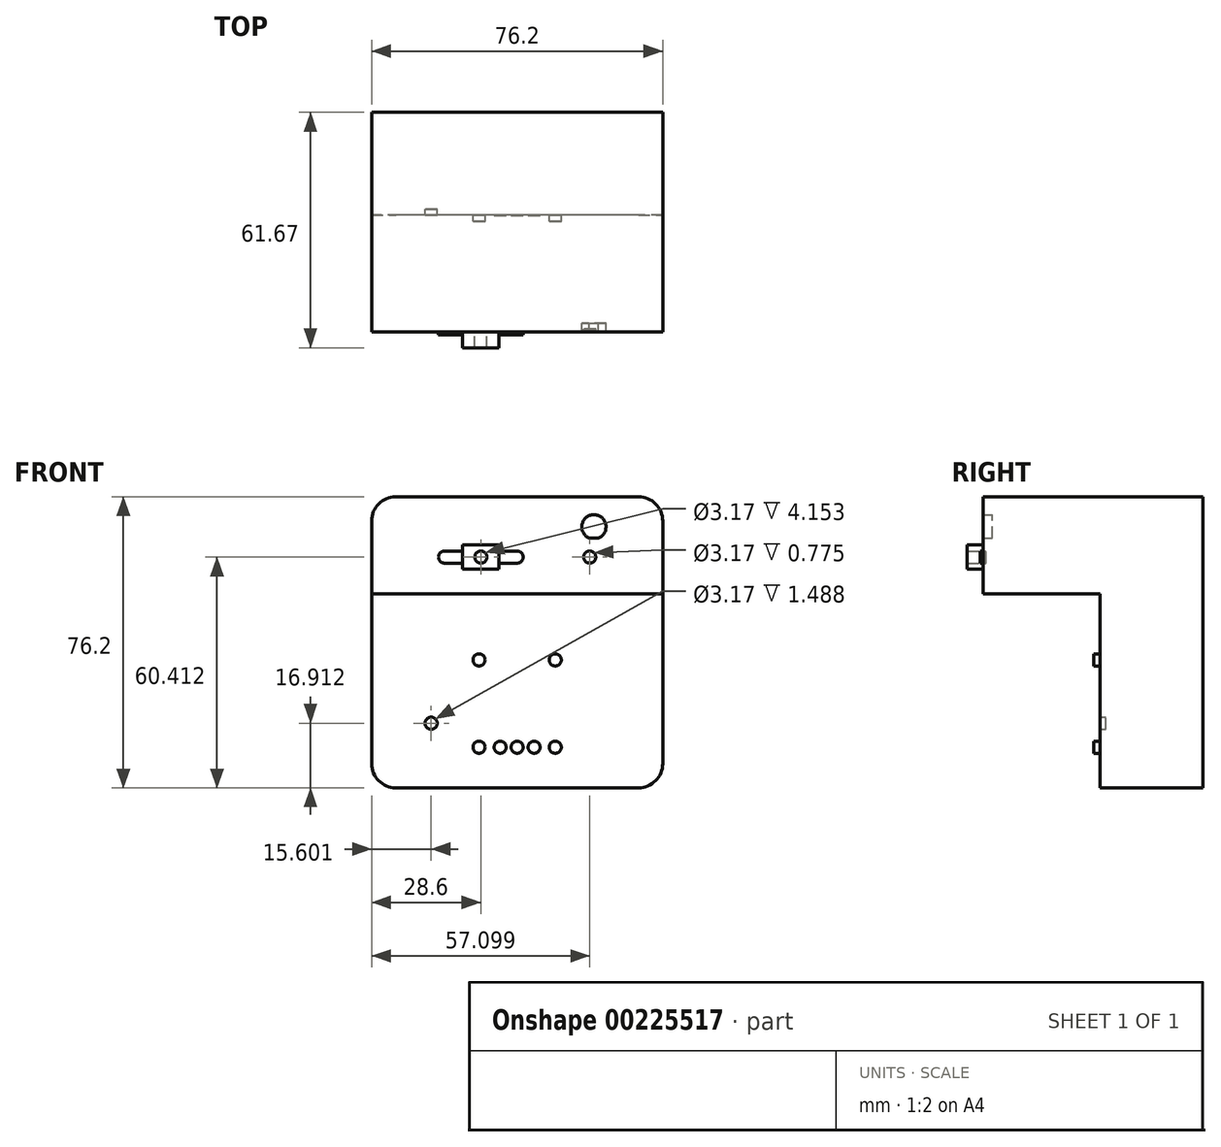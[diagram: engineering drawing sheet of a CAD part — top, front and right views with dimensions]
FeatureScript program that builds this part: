
annotation { "Feature Type Name" : "Feature", "Feature Type Description" : "" }
export const myFeature = defineFeature(function(context is Context, id is Id, definition is map)
    precondition{}
    {
        {
            var Q0;
            Q0=qCreatedBy(makeId("Front.planeOp"),FACE);
            var sketch = newSketch(context, id + "F0", { "sketchPlane" : qUnion([Q0])});
            skLineSegment(sketch, "E0.bottom", {"start": v(38.1, -38.1) * mm, "end": v(-38.1, -38.1) * mm});
            skLineSegment(sketch, "E0.top", {"start": v(38.1, 38.1) * mm, "end": v(-38.1, 38.1) * mm});
            skLineSegment(sketch, "E0.left", {"start": v(38.1, -38.1) * mm, "end": v(38.1, 38.1) * mm});
            skLineSegment(sketch, "E0.right", {"start": v(-38.1, -38.1) * mm, "end": v(-38.1, 38.1) * mm});
            skPoint(sketch, "E0.middle", {"position": v(0, 0) * mm});
            skCircle(sketch, "E1", {"center": v(0, 22.31) * mm, "radius": 1.59 * mm});
            skCircle(sketch, "E2", {"center": v(-19, 22.31) * mm, "radius": 1.59 * mm});
            skCircle(sketch, "E3.MirrorC", {"center": v(19, 22.31) * mm, "radius": 1.59 * mm});
            skLineSegment(sketch, "E4", {"start": v(0, 38.1) * mm, "end": v(0, -38.1) * mm, "construction": true});
            skLineSegment(sketch, "E5", {"start": v(-19, 22.31) * mm, "end": v(19, 22.31) * mm, "construction": true});
            skCircle(sketch, "E6", {"center": v(-4.45, -27.48) * mm, "radius": 1.59 * mm});
            skLineSegment(sketch, "E7.0", {"start": v(-9.5, 38.1) * mm, "end": v(-9.5, -38.1) * mm, "construction": true});
            skCircle(sketch, "E8", {"center": v(-9.98, -27.48) * mm, "radius": 1.59 * mm});
            skCircle(sketch, "E9", {"center": v(-9.98, -4.62) * mm, "radius": 1.59 * mm});
            skLineSegment(sketch, "E10.MirrorCS", {"start": v(9.5, 38.1) * mm, "end": v(9.5, -38.1) * mm, "construction": true});
            skCircle(sketch, "E11.MirrorC", {"center": v(9.98, -4.62) * mm, "radius": 1.59 * mm});
            skCircle(sketch, "E12.MirrorC", {"center": v(9.98, -27.48) * mm, "radius": 1.59 * mm});
            skCircle(sketch, "E13.MirrorC", {"center": v(4.45, -27.48) * mm, "radius": 1.59 * mm});
            skLineSegment(sketch, "E14", {"start": v(-8.39, -27.48) * mm, "end": v(-8.39, -4.62) * mm, "construction": true});
            skLineSegment(sketch, "E15", {"start": v(-38.1, 0) * mm, "end": v(38.1, 0) * mm});
            skSolve(sketch);
        }
        {
            var Q0;
            {var subQ1=sQuery(id+"F0.wireOp",EDGE,"E0.bottom");Q0=makeQuery(id+"F0.imprint","IMPRINT",FACE,{"disambiguationData":[TD([[makeQuery(id+"F0.imprint","IMPRINT",EDGE,{"derivedFrom":subQ1}),-1.0]])]});}
            var Q1;
            {var subQ1=sQuery(id+"F0.wireOp",EDGE,"E0.top");Q1=makeQuery(id+"F0.imprint","IMPRINT",FACE,{"disambiguationData":[TD([[makeQuery(id+"F0.imprint","IMPRINT",EDGE,{"derivedFrom":subQ1}),1.0]])]});}
            extrude(context, id + "F1", {"entities" : qUnion([Q0, Q1]), "oppositeDirection" : true, "depth" : 25.4 * mm});
        }
        {
            var Q0;
            Q0=qCreatedBy(makeId("Front.planeOp"),FACE);
            var sketch = newSketch(context, id + "F2", { "sketchPlane" : qUnion([Q0])});
            skCircle(sketch, "E16.0", {"center": v(-9.98, -4.62) * mm, "radius": 1.59 * mm});
            skCircle(sketch, "E17.0", {"center": v(9.98, -4.62) * mm, "radius": 1.59 * mm});
            skCircle(sketch, "E18.0", {"center": v(9.98, -27.48) * mm, "radius": 1.59 * mm});
            skCircle(sketch, "E19.0", {"center": v(4.45, -27.48) * mm, "radius": 1.59 * mm});
            skCircle(sketch, "E20.0", {"center": v(-4.45, -27.48) * mm, "radius": 1.59 * mm});
            skCircle(sketch, "E21.0", {"center": v(-9.98, -27.48) * mm, "radius": 1.59 * mm});
            skSolve(sketch);
        }
        {
            var Q0;
            Q0=makeQuery(id+"F2.imprint","IMPRINT",FACE,{"disambiguationData":[TD([[makeQuery(id+"F2.imprint","IMPRINT",EDGE,{"derivedFrom":sQuery(id+"F2.wireOp",EDGE,"E17.0")}),1.0]])]});
            var Q1;
            Q1=makeQuery(id+"F2.imprint","IMPRINT",FACE,{"disambiguationData":[TD([[makeQuery(id+"F2.imprint","IMPRINT",EDGE,{"derivedFrom":sQuery(id+"F2.wireOp",EDGE,"E16.0")}),1.0]])]});
            var Q2;
            Q2=makeQuery(id+"F2.imprint","IMPRINT",FACE,{"disambiguationData":[TD([[makeQuery(id+"F2.imprint","IMPRINT",EDGE,{"derivedFrom":sQuery(id+"F2.wireOp",EDGE,"E21.0")}),1.0]])]});
            var Q3;
            Q3=makeQuery(id+"F2.imprint","IMPRINT",FACE,{"disambiguationData":[TD([[makeQuery(id+"F2.imprint","IMPRINT",EDGE,{"derivedFrom":sQuery(id+"F2.wireOp",EDGE,"E20.0")}),1.0]])]});
            var Q4;
            Q4=makeQuery(id+"F2.imprint","IMPRINT",FACE,{"disambiguationData":[TD([[makeQuery(id+"F2.imprint","IMPRINT",EDGE,{"derivedFrom":sQuery(id+"F2.wireOp",EDGE,"E19.0")}),1.0]])]});
            var Q5;
            Q5=makeQuery(id+"F2.imprint","IMPRINT",FACE,{"disambiguationData":[TD([[makeQuery(id+"F2.imprint","IMPRINT",EDGE,{"derivedFrom":sQuery(id+"F2.wireOp",EDGE,"E18.0")}),1.0]])]});
            extrude(context, id + "F3", {"entities" : qUnion([Q0, Q1, Q2, Q3, Q4, Q5]), "operationType" : NewBodyOperationType.ADD, "depth" : 1.59 * mm});
        }
        {
            var Q0;
            Q0=qCreatedBy(makeId("Front.planeOp"),FACE);
            var sketch = newSketch(context, id + "F4", { "sketchPlane" : qUnion([Q0])});
            skCircle(sketch, "E22.0", {"center": v(-19, 22.31) * mm, "radius": 1.59 * mm});
            skCircle(sketch, "E23.0", {"center": v(0, 22.31) * mm, "radius": 1.59 * mm});
            skCircle(sketch, "E24.0", {"center": v(19, 22.31) * mm, "radius": 1.59 * mm});
            skSolve(sketch);
        }
        {
            var Q0;
            Q0 = qSketchRegion(id + "F4", true);
            extrude(context, id + "F5", {"entities" : qUnion([Q0]), "operationType" : NewBodyOperationType.ADD, "depth" : 31.35 * mm});
        }
        {
            var Q0;
            Q0=qCreatedBy(makeId("Front.planeOp"),FACE);
            var sketch = newSketch(context, id + "F6", { "sketchPlane" : qUnion([Q0])});
            skLineSegment(sketch, "E25.0", {"start": v(38.1, 38.1) * mm, "end": v(-38.1, 38.1) * mm});
            skLineSegment(sketch, "E26.0", {"start": v(-38.1, -38.1) * mm, "end": v(-38.1, 38.1) * mm});
            skLineSegment(sketch, "E27.0", {"start": v(38.1, -38.1) * mm, "end": v(38.1, 38.1) * mm});
            skLineSegment(sketch, "E28", {"start": v(-38.1, 0) * mm, "end": v(38.1, 0) * mm});
            skSolve(sketch);
        }
        {
            var Q0;
            {var subQ0=sQuery(id+"F6.wireOp",EDGE,"E25.0");Q0=makeQuery(id+"F6.imprint","IMPRINT",FACE,{"disambiguationData":[TD([[makeQuery(id+"F6.imprint","IMPRINT",EDGE,{"derivedFrom":subQ0}),1.0]])]});}
            extrude(context, id + "F7", {"entities" : qUnion([Q0]), "operationType" : NewBodyOperationType.ADD, "depth" : 29.76 * mm});
        }
        {
            var Q0;
            Q0=makeQuery(id+"F3.opExtrude","CAP_FACE",FACE,{"disambiguationData":[OSD([sQuery(id+"F2.wireOp",EDGE,"E21.0")])],"isStart":false});
            var sketch = newSketch(context, id + "F8", { "sketchPlane" : qUnion([Q0])});
            skCircle(sketch, "E29.0", {"center": v(-9.98, -27.48) * mm, "radius": 1.59 * mm});
            skCircle(sketch, "E30.0.0", {"center": v(-9.98, -4.62) * mm, "radius": 1.59 * mm});
            skCircle(sketch, "E31.0.0", {"center": v(9.98, -4.62) * mm, "radius": 1.59 * mm});
            skCircle(sketch, "E32.0.0", {"center": v(9.98, -27.48) * mm, "radius": 1.59 * mm});
            skSolve(sketch);
        }
        {
            var Q0;
            Q0=makeQuery(id+"F8.imprint","IMPRINT",FACE,{"disambiguationData":[TD([[makeQuery(id+"F8.imprint","IMPRINT",EDGE,{"derivedFrom":sQuery(id+"F8.wireOp",EDGE,"E30.0.0")}),1.0]])]});
            var Q1;
            Q1=makeQuery(id+"F8.imprint","IMPRINT",FACE,{"disambiguationData":[TD([[makeQuery(id+"F8.imprint","IMPRINT",EDGE,{"derivedFrom":sQuery(id+"F8.wireOp",EDGE,"E29.0")}),1.0]])]});
            var Q2;
            Q2=makeQuery(id+"F8.imprint","IMPRINT",FACE,{"disambiguationData":[TD([[makeQuery(id+"F8.imprint","IMPRINT",EDGE,{"derivedFrom":sQuery(id+"F8.wireOp",EDGE,"E32.0.0")}),1.0]])]});
            var Q3;
            Q3=makeQuery(id+"F8.imprint","IMPRINT",FACE,{"disambiguationData":[TD([[makeQuery(id+"F8.imprint","IMPRINT",EDGE,{"derivedFrom":sQuery(id+"F8.wireOp",EDGE,"E31.0.0")}),1.0]])]});
            extrude(context, id + "F9", {"entities" : qUnion([Q0, Q1, Q2, Q3]), "operationType" : NewBodyOperationType.ADD, "depth" : 1.59 * mm});
        }
        {
            var Q0;
            Q0=makeQuery(id+"F1.opExtrude","CAP_FACE",FACE,{"disambiguationData":[OSD([sQuery(id+"F0.wireOp",EDGE,"E0.bottom"),sQuery(id+"F0.wireOp",EDGE,"E0.top"),sQuery(id+"F0.wireOp",EDGE,"E0.left"),sQuery(id+"F0.wireOp",EDGE,"E0.right"),sQuery(id+"F0.wireOp",EDGE,"E1"),sQuery(id+"F0.wireOp",EDGE,"E2"),sQuery(id+"F0.wireOp",EDGE,"E3.MirrorC"),sQuery(id+"F0.wireOp",EDGE,"E6"),sQuery(id+"F0.wireOp",EDGE,"E8"),sQuery(id+"F0.wireOp",EDGE,"E9"),sQuery(id+"F0.wireOp",EDGE,"E11.MirrorC"),sQuery(id+"F0.wireOp",EDGE,"E12.MirrorC"),sQuery(id+"F0.wireOp",EDGE,"E13.MirrorC")])],"isStart":false});
            var sketch = newSketch(context, id + "F10", { "sketchPlane" : qUnion([Q0])});
            skCircle(sketch, "E33.0", {"center": v(9.98, -27.48) * mm, "radius": 1.59 * mm});
            skCircle(sketch, "E34.0", {"center": v(4.45, -27.48) * mm, "radius": 1.59 * mm});
            skCircle(sketch, "E35.0", {"center": v(-4.45, -27.48) * mm, "radius": 1.59 * mm});
            skCircle(sketch, "E36.0", {"center": v(-9.98, -27.48) * mm, "radius": 1.59 * mm});
            skCircle(sketch, "E37.0", {"center": v(9.98, -4.62) * mm, "radius": 1.59 * mm});
            skCircle(sketch, "E38.0", {"center": v(-9.98, -4.62) * mm, "radius": 1.59 * mm});
            skCircle(sketch, "E39.0", {"center": v(19, 22.31) * mm, "radius": 1.59 * mm});
            skCircle(sketch, "E40.0", {"center": v(0, 22.31) * mm, "radius": 1.59 * mm});
            skCircle(sketch, "E41.0", {"center": v(-19, 22.31) * mm, "radius": 1.59 * mm});
            skSolve(sketch);
        }
        {
            var Q0;
            Q0 = qSketchRegion(id + "F10", true);
            extrude(context, id + "F11", {"entities" : qUnion([Q0]), "operationType" : NewBodyOperationType.ADD, "endBound" : BoundingType.UP_TO_NEXT, "oppositeDirection" : true, "depth" : 25.4 * mm});
        }
        {
            var Q0;
            Q0=makeQuery(id+"F7.opExtrude","CAP_FACE",FACE,{"disambiguationData":[OSD([sQuery(id+"F6.wireOp",EDGE,"E25.0"),sQuery(id+"F6.wireOp",EDGE,"E26.0"),sQuery(id+"F6.wireOp",EDGE,"E27.0"),sQuery(id+"F6.wireOp",EDGE,"E28")])],"isStart":false});
            var sketch = newSketch(context, id + "F12", { "sketchPlane" : qUnion([Q0])});
            skLineSegment(sketch, "E42.0", {"start": v(-38.1, 0) * mm, "end": v(38.1, 0) * mm});
            skLineSegment(sketch, "E43.0", {"start": v(-38.1, 0) * mm, "end": v(-38.1, 12.7) * mm});
            skLineSegment(sketch, "E44.0", {"start": v(38.1, 0) * mm, "end": v(38.1, 12.7) * mm});
            skLineSegment(sketch, "E45", {"start": v(-38.1, 12.7) * mm, "end": v(38.1, 12.7) * mm});
            skPoint(sketch, "E46.orphan", {"position": v(-38.1, 38.1) * mm});
            skPoint(sketch, "E47.orphan", {"position": v(38.1, 38.1) * mm});
            skSolve(sketch);
        }
        {
            var Q0;
            Q0=makeQuery(id+"F12.imprint","IMPRINT",FACE,{"disambiguationData":[TD([[makeQuery(id+"F12.imprint","IMPRINT",EDGE,{"derivedFrom":sQuery(id+"F12.wireOp",EDGE,"E42.0")}),1.0]])]});
            var Q1;
            Q1=makeQuery(id+"F1.opExtrude","CAP_FACE",FACE,{"disambiguationData":[OSD([sQuery(id+"F0.wireOp",EDGE,"E0.bottom"),sQuery(id+"F0.wireOp",EDGE,"E0.top"),sQuery(id+"F0.wireOp",EDGE,"E0.left"),sQuery(id+"F0.wireOp",EDGE,"E0.right"),sQuery(id+"F0.wireOp",EDGE,"E1"),sQuery(id+"F0.wireOp",EDGE,"E2"),sQuery(id+"F0.wireOp",EDGE,"E3.MirrorC"),sQuery(id+"F0.wireOp",EDGE,"E6"),sQuery(id+"F0.wireOp",EDGE,"E8"),sQuery(id+"F0.wireOp",EDGE,"E9"),sQuery(id+"F0.wireOp",EDGE,"E11.MirrorC"),sQuery(id+"F0.wireOp",EDGE,"E12.MirrorC"),sQuery(id+"F0.wireOp",EDGE,"E13.MirrorC")])],"isStart":true});
            extrude(context, id + "F13", {"entities" : qUnion([Q0]), "operationType" : NewBodyOperationType.REMOVE, "endBound" : BoundingType.UP_TO_SURFACE, "oppositeDirection" : true, "endBoundEntityFace" : qUnion([Q1]), "depth" : 25.4 * mm});
        }
        {
            var Q0;
            Q0=makeQuery(id+"F1.opExtrude","SWEPT_EDGE",EDGE,{"disambiguationData":[OSD([sQuery(id+"F0.wireOp",EDGE,"E0.bottom"),sQuery(id+"F0.wireOp",EDGE,"E0.right")])]});
            var Q1;
            Q1=makeQuery(id+"F1.opExtrude","SWEPT_EDGE",EDGE,{"disambiguationData":[OSD([sQuery(id+"F0.wireOp",EDGE,"E0.bottom"),sQuery(id+"F0.wireOp",EDGE,"E0.left")])]});
            var Q2;
            Q2=makeQuery(id+"F7.opExtrude","SWEPT_EDGE",EDGE,{"disambiguationData":[OSD([sQuery(id+"F6.wireOp",EDGE,"E27.0"),sQuery(id+"F6.wireOp",EDGE,"E28")])]});
            var Q3;
            Q3=makeQuery(id+"F7.boolean.opBoolean","MERGE",EDGE,{"derivedFrom":[makeQuery(id+"F1.opExtrude","SWEPT_EDGE",EDGE,{"disambiguationData":[OSD([sQuery(id+"F0.wireOp",EDGE,"E0.top"),sQuery(id+"F0.wireOp",EDGE,"E0.left")])]}),makeQuery(id+"F7.opExtrude","SWEPT_EDGE",EDGE,{"disambiguationData":[OSD([sQuery(id+"F6.wireOp",EDGE,"E25.0"),sQuery(id+"F6.wireOp",EDGE,"E27.0")])]})]});
            var Q4;
            Q4=makeQuery(id+"F7.opExtrude","SWEPT_EDGE",EDGE,{"disambiguationData":[OSD([sQuery(id+"F6.wireOp",EDGE,"E26.0"),sQuery(id+"F6.wireOp",EDGE,"E28")])]});
            var Q5;
            Q5=makeQuery(id+"F7.boolean.opBoolean","MERGE",EDGE,{"derivedFrom":[makeQuery(id+"F1.opExtrude","SWEPT_EDGE",EDGE,{"disambiguationData":[OSD([sQuery(id+"F0.wireOp",EDGE,"E0.top"),sQuery(id+"F0.wireOp",EDGE,"E0.right")])]}),makeQuery(id+"F7.opExtrude","SWEPT_EDGE",EDGE,{"disambiguationData":[OSD([sQuery(id+"F6.wireOp",EDGE,"E25.0"),sQuery(id+"F6.wireOp",EDGE,"E26.0")])]})]});
            var Q6;
            Q6=makeQuery(id+"F13.boolean.opBoolean","COPY",EDGE,{"derivedFrom":makeQuery(id+"F13.opExtrude","SWEPT_EDGE",EDGE,{"disambiguationData":[OSD([sQuery(id+"F6.wireOp",EDGE,"E26.0"),sQuery(id+"F12.wireOp",EDGE,"E43.0"),sQuery(id+"F12.wireOp",EDGE,"E45")])]})});
            var Q7;
            Q7=makeQuery(id+"F13.boolean.opBoolean","COPY",EDGE,{"derivedFrom":makeQuery(id+"F13.opExtrude","SWEPT_EDGE",EDGE,{"disambiguationData":[OSD([sQuery(id+"F6.wireOp",EDGE,"E27.0"),sQuery(id+"F12.wireOp",EDGE,"E44.0"),sQuery(id+"F12.wireOp",EDGE,"E45")])]})});
            fillet(context, id + "F14", {"entities" : qUnion([Q0, Q1, Q2, Q3, Q4, Q5, Q6, Q7]), "radius" : 6.35 * mm, "tangentPropagation" : true, "allowEdgeOverflow" : false});
        }
        {
            var Q0;
            Q0=makeQuery(id+"F5.opExtrude","CAP_FACE",FACE,{"disambiguationData":[OSD([sQuery(id+"F4.wireOp",EDGE,"E22.0")])],"isStart":false});
            var sketch = newSketch(context, id + "F15", { "sketchPlane" : qUnion([Q0])});
            skArc(sketch, "E48", {"start": v(0, 20.72) * mm, "mid": v(1.59, 22.31) * mm, "end": v(0, 23.9) * mm});
            skLineSegment(sketch, "E49", {"start": v(-19, 23.9) * mm, "end": v(-14.26, 23.9) * mm});
            skLineSegment(sketch, "E50", {"start": v(-19, 20.72) * mm, "end": v(-14.26, 20.72) * mm});
            skLineSegment(sketch, "E51", {"start": v(-19, 22.31) * mm, "end": v(0, 22.31) * mm, "construction": true});
            skLineSegment(sketch, "E52.0", {"start": v(-14.26, 19.14) * mm, "end": v(-4.74, 19.14) * mm});
            skLineSegment(sketch, "E53", {"start": v(-9.5, 25.49) * mm, "end": v(-9.5, 19.14) * mm});
            skPoint(sketch, "E53.startSnap0", {"position": v(-9.5, 22.31) * mm});
            skLineSegment(sketch, "E54.0", {"start": v(-14.26, 25.49) * mm, "end": v(-4.74, 25.49) * mm});
            skLineSegment(sketch, "E55.0", {"start": v(-14.26, 25.49) * mm, "end": v(-14.26, 23.9) * mm});
            skLineSegment(sketch, "E56.0", {"start": v(-4.74, 25.49) * mm, "end": v(-4.74, 23.9) * mm});
            skPoint(sketch, "E57.orphan", {"position": v(-9.5, 27.07) * mm});
            skLineSegment(sketch, "E58.trimOffspring", {"start": v(-4.74, 23.9) * mm, "end": v(0, 23.9) * mm});
            skLineSegment(sketch, "E59.trimOffspring", {"start": v(-4.74, 20.72) * mm, "end": v(0, 20.72) * mm});
            skLineSegment(sketch, "E60.trimOffspring", {"start": v(-14.26, 20.72) * mm, "end": v(-14.26, 19.14) * mm});
            skLineSegment(sketch, "E61.trimOffspring", {"start": v(-4.74, 20.72) * mm, "end": v(-4.74, 19.14) * mm});
            skCircle(sketch, "E62", {"center": v(-9.5, 22.31) * mm, "radius": 1.59 * mm});
            skSolve(sketch);
        }
        {
            var Q0;
            {var subQ10=sQuery(id+"F15.wireOp",EDGE,"E49");Q0=makeQuery(id+"F15.imprint","IMPRINT",FACE,{"disambiguationData":[TD([[makeQuery(id+"F15.imprint","IMPRINT",EDGE,{"derivedFrom":subQ10}),-1.0]])]});}
            var Q1;
            Q1=makeQuery(id+"F15.imprint","IMPRINT",FACE,{"disambiguationData":[TD([[makeQuery(id+"F15.imprint","IMPRINT",EDGE,{"derivedFrom":sQuery(id+"F15.wireOp",EDGE,"E48")}),1.0]])]});
            var Q2;
            {var subQ0=makeQuery(id+"F5.opExtrude","CAP_EDGE",EDGE,{"disambiguationData":[OSD([sQuery(id+"F4.wireOp",EDGE,"E22.0")])],"isStart":false});var subQ1=makeQuery(id+"F15.imprint","INTERSECT",VERTEX,{"derivedFrom":[subQ0,sQuery(id+"F15.wireOp",EDGE,"E49")]});Q2=makeQuery(id+"F15.imprint","IMPRINT",FACE,{"disambiguationData":[TD([[makeQuery(id+"F15.imprint","IMPRINT",EDGE,{"disambiguationData":[TD([[subQ1,-1.0]])],"derivedFrom":subQ0}),1.0]])]});}
            extrude(context, id + "F16", {"entities" : qUnion([Q0, Q1, Q2]), "depth" : 1.57 * mm});
        }
        {
            var Q0;
            {var subQ0=sQuery(id+"F4.wireOp",EDGE,"E22.0");Q0=makeQuery(id+"F16.boolean.opBoolean","MERGE",FACE,{"derivedFrom":[makeQuery(id+"F5.opExtrude","CAP_FACE",FACE,{"disambiguationData":[OSD([subQ0])],"isStart":false}),makeQuery(id+"F5.opExtrude","CAP_FACE",FACE,{"disambiguationData":[OSD([sQuery(id+"F4.wireOp",EDGE,"E23.0")])],"isStart":false}),makeQuery(id+"F16.opExtrude","CAP_FACE",FACE,{"disambiguationData":[OSD([subQ0,sQuery(id+"F15.wireOp",EDGE,"E48"),sQuery(id+"F15.wireOp",EDGE,"E49"),sQuery(id+"F15.wireOp",EDGE,"E50"),sQuery(id+"F15.wireOp",EDGE,"E52.0"),sQuery(id+"F15.wireOp",EDGE,"E54.0"),sQuery(id+"F15.wireOp",EDGE,"E55.0"),sQuery(id+"F15.wireOp",EDGE,"E56.0"),sQuery(id+"F15.wireOp",EDGE,"E58.trimOffspring"),sQuery(id+"F15.wireOp",EDGE,"E59.trimOffspring"),sQuery(id+"F15.wireOp",EDGE,"E60.trimOffspring"),sQuery(id+"F15.wireOp",EDGE,"E61.trimOffspring"),sQuery(id+"F15.wireOp",EDGE,"E62")])],"isStart":true})]});}
            var sketch = newSketch(context, id + "F17", { "sketchPlane" : qUnion([Q0])});
            skCircle(sketch, "E63.0", {"center": v(-9.5, 22.31) * mm, "radius": 1.59 * mm});
            skLineSegment(sketch, "E64.0", {"start": v(-4.74, 25.49) * mm, "end": v(-14.26, 25.49) * mm});
            skLineSegment(sketch, "E65.0", {"start": v(-4.74, 19.14) * mm, "end": v(-14.26, 19.14) * mm});
            skLineSegment(sketch, "E66", {"start": v(-14.26, 25.49) * mm, "end": v(-14.26, 19.14) * mm});
            skLineSegment(sketch, "E67", {"start": v(-4.74, 25.49) * mm, "end": v(-4.74, 19.14) * mm});
            skSolve(sketch);
        }
        {
            var Q0;
            Q0=makeQuery(id+"F17.imprint","IMPRINT",FACE,{"disambiguationData":[TD([[makeQuery(id+"F17.imprint","IMPRINT",EDGE,{"derivedFrom":sQuery(id+"F17.wireOp",EDGE,"E63.0")}),-1.0]])]});
            extrude(context, id + "F18", {"entities" : qUnion([Q0]), "operationType" : NewBodyOperationType.ADD, "depth" : 4.93 * mm});
        }
        {
            var Q0;
            {var subQ0=sQuery(id+"F0.wireOp",EDGE,"E13.MirrorC");var subQ1=sQuery(id+"F0.wireOp",EDGE,"E12.MirrorC");var subQ2=sQuery(id+"F0.wireOp",EDGE,"E11.MirrorC");var subQ3=sQuery(id+"F0.wireOp",EDGE,"E9");var subQ4=sQuery(id+"F0.wireOp",EDGE,"E8");var subQ5=sQuery(id+"F0.wireOp",EDGE,"E6");var subQ6=sQuery(id+"F0.wireOp",EDGE,"E3.MirrorC");var subQ7=sQuery(id+"F0.wireOp",EDGE,"E2");var subQ8=sQuery(id+"F0.wireOp",EDGE,"E1");var subQ9=sQuery(id+"F0.wireOp",EDGE,"E0.right");var subQ10=sQuery(id+"F0.wireOp",EDGE,"E0.left");var subQ11=sQuery(id+"F0.wireOp",EDGE,"E0.top");var subQ12=sQuery(id+"F0.wireOp",EDGE,"E0.bottom");Q0=makeQuery(id+"F13.boolean.opBoolean","MERGE",FACE,{"derivedFrom":[makeQuery(id+"F1.opExtrude","CAP_FACE",FACE,{"disambiguationData":[OSD([subQ12,subQ11,subQ10,subQ9,subQ8,subQ7,subQ6,subQ5,subQ4,subQ3,subQ2,subQ1,subQ0])],"isStart":true}),makeQuery(id+"F13.opExtrude","CAP_FACE",FACE,{"disambiguationData":[OSD([subQ12,subQ11,subQ10,subQ9,subQ8,subQ7,subQ6,subQ5,subQ4,subQ3,subQ2,subQ1,subQ0])],"isStart":false})]});}
            var sketch = newSketch(context, id + "F19", { "sketchPlane" : qUnion([Q0])});
            skPoint(sketch, "E68.0", {"position": v(-9.98, -27.48) * mm});
            skPoint(sketch, "E69.0", {"position": v(9.98, -27.48) * mm});
            skLineSegment(sketch, "E70", {"start": v(-9.98, -27.48) * mm, "end": v(9.98, -27.48) * mm, "construction": true});
            skCircle(sketch, "E71", {"center": v(0, -27.48) * mm, "radius": 1.59 * mm});
            skSolve(sketch);
        }
        {
            var Q0;
            Q0=makeQuery(id+"F19.imprint","IMPRINT",FACE,{"disambiguationData":[TD([[makeQuery(id+"F19.imprint","IMPRINT",EDGE,{"derivedFrom":sQuery(id+"F19.wireOp",EDGE,"E71")}),1.0]])]});
            extrude(context, id + "F20", {"entities" : qUnion([Q0]), "operationType" : NewBodyOperationType.ADD, "depth" : 1.59 * mm});
        }
        {
            var Q0;
            Q0=makeQuery(id+"F7.opExtrude","CAP_FACE",FACE,{"disambiguationData":[OSD([sQuery(id+"F6.wireOp",EDGE,"E25.0"),sQuery(id+"F6.wireOp",EDGE,"E26.0"),sQuery(id+"F6.wireOp",EDGE,"E27.0"),sQuery(id+"F6.wireOp",EDGE,"E28")])],"isStart":false});
            var sketch = newSketch(context, id + "F21", { "sketchPlane" : qUnion([Q0])});
            skArc(sketch, "E72.0", {"start": v(-19, 23.9) * mm, "mid": v(-20.59, 22.31) * mm, "end": v(-19, 20.72) * mm});
            skArc(sketch, "E73.0", {"start": v(0, 20.72) * mm, "mid": v(1.59, 22.31) * mm, "end": v(0, 23.9) * mm});
            skLineSegment(sketch, "E74", {"start": v(-19, 22.31) * mm, "end": v(0, 22.31) * mm, "construction": true});
            skLineSegment(sketch, "E75", {"start": v(-9.5, 22.31) * mm, "end": v(-9.5, 12.7) * mm, "construction": true});
            skArc(sketch, "E76", {"start": v(-18.86, 27.31) * mm, "mid": v(-20.1, 33.41) * mm, "end": v(-21.32, 27.31) * mm});
            skLineSegment(sketch, "E77", {"start": v(0, 22.31) * mm, "end": v(0, 0) * mm, "construction": true});
            skArc(sketch, "E78.MirrorC", {"start": v(18.86, 27.31) * mm, "mid": v(20.1, 33.41) * mm, "end": v(21.32, 27.31) * mm});
            skLineSegment(sketch, "E79.0", {"start": v(-21.32, 27.31) * mm, "end": v(-18.86, 27.31) * mm});
            skArc(sketch, "E80", {"start": v(1.23, 27.31) * mm, "mid": v(0, 33.41) * mm, "end": v(-1.23, 27.31) * mm});
            skLineSegment(sketch, "E81", {"start": v(-20.1, 30.24) * mm, "end": v(20.1, 30.24) * mm, "construction": true});
            skLineSegment(sketch, "E82.trimOffspring", {"start": v(-1.23, 27.31) * mm, "end": v(1.23, 27.31) * mm});
            skLineSegment(sketch, "E83.trimOffspring", {"start": v(18.86, 27.31) * mm, "end": v(21.32, 27.31) * mm});
            skSolve(sketch);
        }
        {
            var Q0;
            Q0=makeQuery(id+"F21.imprint","IMPRINT",FACE,{"disambiguationData":[TD([[makeQuery(id+"F21.imprint","IMPRINT",EDGE,{"derivedFrom":sQuery(id+"F21.wireOp",EDGE,"f5aa9148-bf45-40ce-b2a6-bb95141deb4a0.MirrorC")}),-1.0]])]});
            var Q1;
            Q1=makeQuery(id+"F21.imprint","IMPRINT",FACE,{"disambiguationData":[TD([[makeQuery(id+"F21.imprint","IMPRINT",EDGE,{"derivedFrom":sQuery(id+"F21.wireOp",EDGE,"E78.MirrorC")}),-1.0]])]});
            var Q2;
            Q2=makeQuery(id+"F21.imprint","IMPRINT",FACE,{"disambiguationData":[TD([[makeQuery(id+"F21.imprint","IMPRINT",EDGE,{"derivedFrom":sQuery(id+"F21.wireOp",EDGE,"E76")}),1.0]])]});
            var Q3;
            Q3=makeQuery(id+"F21.imprint","IMPRINT",FACE,{"disambiguationData":[TD([[makeQuery(id+"F21.imprint","IMPRINT",EDGE,{"derivedFrom":sQuery(id+"F21.wireOp",EDGE,"E80")}),1.0]])]});
            extrude(context, id + "F22", {"entities" : qUnion([Q0, Q1, Q2, Q3]), "operationType" : NewBodyOperationType.ADD, "depth" : 2.36 * mm});
        }
        {
            var Q0;
            {var subQ0=sQuery(id+"F0.wireOp",EDGE,"E13.MirrorC");var subQ1=sQuery(id+"F0.wireOp",EDGE,"E12.MirrorC");var subQ2=sQuery(id+"F0.wireOp",EDGE,"E11.MirrorC");var subQ3=sQuery(id+"F0.wireOp",EDGE,"E9");var subQ4=sQuery(id+"F0.wireOp",EDGE,"E8");var subQ5=sQuery(id+"F0.wireOp",EDGE,"E6");var subQ6=sQuery(id+"F0.wireOp",EDGE,"E3.MirrorC");var subQ7=sQuery(id+"F0.wireOp",EDGE,"E2");var subQ8=sQuery(id+"F0.wireOp",EDGE,"E1");var subQ9=sQuery(id+"F0.wireOp",EDGE,"E0.right");var subQ10=sQuery(id+"F0.wireOp",EDGE,"E0.left");var subQ11=sQuery(id+"F0.wireOp",EDGE,"E0.top");var subQ12=sQuery(id+"F0.wireOp",EDGE,"E0.bottom");Q0=makeQuery(id+"F13.boolean.opBoolean","MERGE",FACE,{"derivedFrom":[makeQuery(id+"F1.opExtrude","CAP_FACE",FACE,{"disambiguationData":[OSD([subQ12,subQ11,subQ10,subQ9,subQ8,subQ7,subQ6,subQ5,subQ4,subQ3,subQ2,subQ1,subQ0])],"isStart":true}),makeQuery(id+"F13.opExtrude","CAP_FACE",FACE,{"disambiguationData":[OSD([subQ12,subQ11,subQ10,subQ9,subQ8,subQ7,subQ6,subQ5,subQ4,subQ3,subQ2,subQ1,subQ0])],"isStart":false})]});}
            var sketch = newSketch(context, id + "F23", { "sketchPlane" : qUnion([Q0])});
            skCircle(sketch, "E84.0", {"center": v(19, 22.31) * mm, "radius": 1.59 * mm});
            skCircle(sketch, "E85.0", {"center": v(-19, 22.31) * mm, "radius": 1.59 * mm});
            skCircle(sketch, "E86", {"center": v(22.5, -21.19) * mm, "radius": 1.59 * mm});
            skLineSegment(sketch, "E87", {"start": v(0, 0) * mm, "end": v(0, -27.48) * mm, "construction": true});
            skCircle(sketch, "E88.MirrorC", {"center": v(-22.5, -21.19) * mm, "radius": 1.59 * mm});
            skSolve(sketch);
        }
        {
            var Q0;
            Q0=makeQuery(id+"F23.imprint","IMPRINT",FACE,{"disambiguationData":[TD([[makeQuery(id+"F23.imprint","IMPRINT",EDGE,{"derivedFrom":sQuery(id+"F23.wireOp",EDGE,"E88.MirrorC")}),-1.0]])]});
            var Q1;
            Q1=makeQuery(id+"F23.imprint","IMPRINT",FACE,{"disambiguationData":[TD([[makeQuery(id+"F23.imprint","IMPRINT",EDGE,{"derivedFrom":sQuery(id+"F23.wireOp",EDGE,"E86")}),1.0]])]});
            extrude(context, id + "F24", {"entities" : qUnion([Q0, Q1]), "operationType" : NewBodyOperationType.ADD, "depth" : 1.49 * mm});
        }
    });
